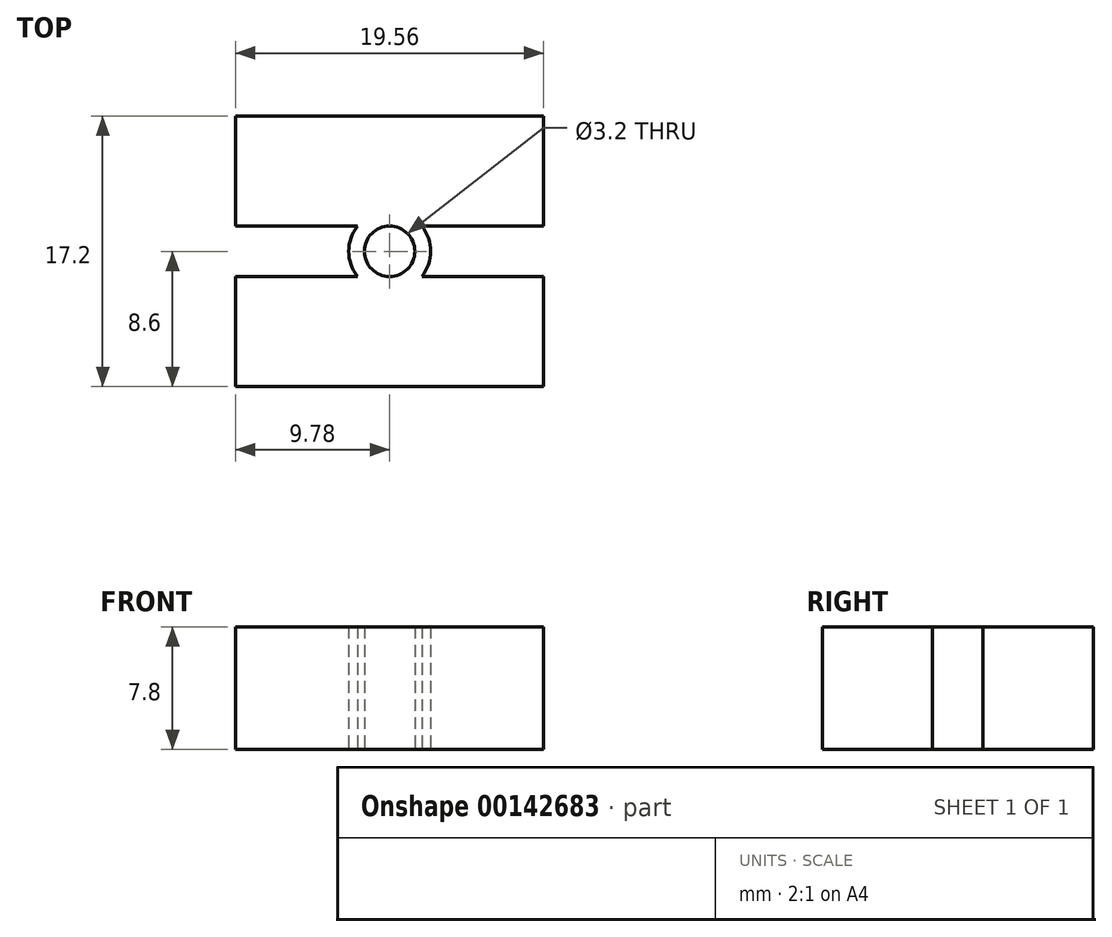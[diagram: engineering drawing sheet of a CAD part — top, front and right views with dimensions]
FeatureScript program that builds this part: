
annotation { "Feature Type Name" : "Feature", "Feature Type Description" : "" }
export const myFeature = defineFeature(function(context is Context, id is Id, definition is map)
    precondition{}
    {
        {
            var Q0;
            Q0=qCreatedBy(makeId("Top.planeOp"),FACE);
            var sketch = newSketch(context, id + "F0", { "sketchPlane" : qUnion([Q0])});
            skLineSegment(sketch, "E0.bottom", {"start": v(9.78, 8.6) * mm, "end": v(-9.77, 8.6) * mm});
            skLineSegment(sketch, "E0.top", {"start": v(9.77, -8.6) * mm, "end": v(-9.78, -8.6) * mm});
            skLineSegment(sketch, "E0.left", {"start": v(9.78, 8.6) * mm, "end": v(9.78, 1.6) * mm});
            skLineSegment(sketch, "E0.right", {"start": v(-9.77, 8.6) * mm, "end": v(-9.77, 1.6) * mm});
            skPoint(sketch, "E0.middle", {"position": v(0, 0) * mm});
            skLineSegment(sketch, "E1", {"start": v(-9.77, 1.6) * mm, "end": v(-2.05, 1.6) * mm, "construction": true});
            skCircle(sketch, "E2", {"center": v(0, 0) * mm, "radius": 1.6 * mm});
            skArc(sketch, "E3", {"start": v(-2.05, 1.6) * mm, "mid": v(-2.6, 0) * mm, "end": v(-2.05, -1.6) * mm});
            skLineSegment(sketch, "E4", {"start": v(-9.77, -1.6) * mm, "end": v(-2.05, -1.6) * mm, "construction": true});
            skLineSegment(sketch, "E5", {"start": v(2.05, -1.6) * mm, "end": v(9.78, -1.6) * mm});
            skLineSegment(sketch, "E6", {"start": v(-2.05, -1.6) * mm, "end": v(-9.77, -1.6) * mm});
            skLineSegment(sketch, "E7", {"start": v(-9.77, 1.6) * mm, "end": v(-2.05, 1.6) * mm});
            skLineSegment(sketch, "E8", {"start": v(9.78, 1.6) * mm, "end": v(2.05, 1.6) * mm});
            skArc(sketch, "E9.trimOffspring", {"start": v(2.05, -1.6) * mm, "mid": v(2.6, 0) * mm, "end": v(2.05, 1.6) * mm});
            skLineSegment(sketch, "E10.trimOffspring", {"start": v(2.05, -1.6) * mm, "end": v(9.78, -1.6) * mm, "construction": true});
            skLineSegment(sketch, "E11.trimOffspring", {"start": v(2.05, 1.6) * mm, "end": v(9.78, 1.6) * mm, "construction": true});
            skLineSegment(sketch, "E12.trimOffspring", {"start": v(-9.77, -1.6) * mm, "end": v(-9.77, -8.6) * mm});
            skLineSegment(sketch, "E13.trimOffspring", {"start": v(9.77, -1.6) * mm, "end": v(9.77, -8.6) * mm});
            skSolve(sketch);
        }
        {
            var Q0;
            Q0 = qSketchRegion(id + "F0", true);
            extrude(context, id + "F1", {"entities" : qUnion([Q0]), "depth" : 7.8 * mm});
        }
    });
